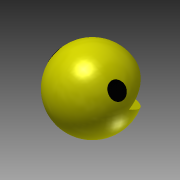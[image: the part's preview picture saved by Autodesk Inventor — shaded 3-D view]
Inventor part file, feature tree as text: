
AUTODESK INVENTOR PART (.ipt)
format: ipt  version: 2015 (Build 190159000, 159)  size: 162,816 bytes
history: native  units: in
note: dims shown in document units (in); Inventor stores cm internally (conversion verified against a paired STEP export)
features: plane x4, sketch x4, revolve x1, extrude x1, emboss x1, mirror x1, projected_geometry x1
ambient origin geometry x8: Origin, YZ Plane, XZ Plane, XY Plane, X Axis, Y Axis, Z Axis, Center Point
bodies: Solid1 (feature_tree)
feature tree (13):
  revolve  "Revolution1"  Angle=90.0deg
  extrude  "Extrusion1"  TaperAngle=120.0deg  [1 undecoded]
  plane  "Work Plane1"
  sketch  "Sketch3"  dims[d4=39.3701in d5=0.0in]
  plane  "Work Plane2"
  emboss  "Emboss1"
  plane  "Work Plane4"
  mirror  "Mirror1"
  sketch  "Sketch1"  dims[d0=39.3701in d1=90.0deg]
  sketch  "Sketch2"  dims[d2=60.0deg d3=120.0deg]
  projected_geometry  "Projected Loop1"
  sketch  "Sketch4"  dims[d6=7.874in d7=0.1in d8=0.0in]
  plane  "Work Plane3"
note: 1 required parameter value undecoded (feature->parameter linkage not recoverable at this tier; creation-order binding heuristic only, values carry confidence <= 0.55)
